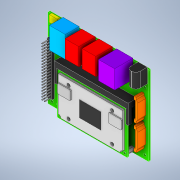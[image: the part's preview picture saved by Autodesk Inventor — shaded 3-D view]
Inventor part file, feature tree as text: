
AUTODESK INVENTOR PART (.ipt)
format: ipt  version: 2022 (Build 260153000, 153)  size: 630,784 bytes
history: native  units: mm
features: extrude x20, sketch x20, other x6, fillet x4, pattern_linear x1
ambient origin geometry x8: Origin, YZ Plane, XZ Plane, XY Plane, X Axis, Y Axis, Z Axis, Center Point
bodies: Solid1 (feature_tree), Solid2 (feature_tree), Solid3 (feature_tree), Solid4 (feature_tree), Solid5 (feature_tree), Solid6 (feature_tree), Solid8 (feature_tree), Solid9 (feature_tree), Solid10 (feature_tree)
feature tree (51):
  extrude  "Extrusion1"  Depth=79.0mm
  extrude  "Extrusion2"  Depth=6.0mm
  fillet  "Fillet1"  Radius=2.75mm
  extrude  "Extrusion3"  Depth=2.75mm
  extrude  "Extrusion4"  Depth=4.0mm
  pattern_linear  "Rectangular Pattern1"  Count1=20 Spacing1=2.54mm
  extrude  "Extrusion5"  Depth=2.75mm
  extrude  "Extrusion6"  Depth=20.2mm
  extrude  "Extrusion7"  Depth=16.2mm
  fillet  "Fillet2"  Radius=3.6mm
  extrude  "Extrusion8"  Depth=3.6mm
  extrude  "Extrusion9"  Depth=4.0mm
  extrude  "Extrusion10"  Depth=4.0mm
  extrude  "Extrusion11"  Depth=6.69mm TaperAngle=0.0deg
  fillet  "Fillet3"  Radius=5.5mm
  extrude  "Extrusion12"  Depth=73.0mm
  extrude  "Extrusion13"  Depth=63.6mm
  extrude  "Extrusion14"  Depth=31.8mm
  extrude  "Extrusion15"  Depth=45.45mm
  extrude  "Extrusion16"  Depth=9.15mm TaperAngle=0.0deg
  extrude  "Extrusion17"  Depth=69.6mm
  extrude  "Extrusion18"  Depth=0.75mm
  extrude  "Extrusion19"  Depth=3.0mm
  extrude  "Extrusion20"  Depth=1.2mm TaperAngle=0.0deg
  fillet  "Fillet4"  Radius=0.6mm
  sketch  "Sketch1"  dims[d0=100.0mm d1=79.0mm]
  sketch  "Sketch2"  dims[d2=1.57mm d3=0.0mm d4=6.0mm d5=2.75mm]
  sketch  "Sketch3"  dims[d6=2.75mm d7=2.75mm]
  sketch  "Sketch4"  dims[d8=4.0mm d9=17.0mm]
  sketch  "Sketch5"  dims[d10=29.0mm]
  sketch  "Sketch6"  dims[d11=4.0mm]
  sketch  "Sketch8"  dims[d12=0.0mm d13=0.0mm]
  sketch  "Sketch9"  dims[d14=0.6mm]
  sketch  "Sketch10"  dims[d15=1.46mm]
  sketch  "Sketch11"  dims[d16=7.46mm]
  sketch  "Sketch12"  dims[d17=5.08mm]
  sketch  "Sketch13"  dims[d18=50.8mm]
  sketch  "Sketch14"  dims[d19=2.54mm d20=0.0mm]
  other  "CAMERA_CONNECTORS"
  sketch  "Sketch15"  dims[d21=0.64mm]
  sketch  "Sketch16"  dims[d22=0.64mm]
  sketch  "Sketch17"  dims[d23=0.95mm]
  other  "USB_MINI"
  sketch  "Sketch18"  dims[d24=0.95mm]
  other  "ETHERNET"
  sketch  "Sketch19"  dims[d25=6.06mm d26=0.0mm d27=200.0mm d29=2.54mm]
  other  "USB"
  sketch  "Sketch20"  dims[d30=20.0mm d32=2.54mm d33=2.75mm]
  other  "HDMI_DISPLAYPORT"
  sketch  "Sketch21"  dims[d34=2.75mm d35=20.2mm d36=16.2mm d37=3.6mm d38=3.6mm d39=4.0mm d40=4.0mm d41=6.69mm d42=0.0mm d43=5.5mm d44=73.0mm d45=63.6mm d46=31.8mm d47=45.45mm d48=9.15mm d49=0.0mm d50=69.6mm d51=0.75mm d52=3.0mm d53=1.2mm d54=0.0mm d55=0.6mm d56=1.26mm d57=1.26mm d58=2.0mm d59=36.5mm d60=73.0mm d61=13.7mm d62=0.0mm d63=5.0mm d64=5.0mm d65=2.7mm d66=2.7mm d67=2.0mm d68=0.0mm d69=21.6mm d70=16.14mm d71=28.67mm d72=24.0mm d73=0.245mm d74=0.0mm d75=15.95mm d76=32.7mm d77=12.6mm d78=9.4mm d79=10.8mm d80=1.0mm d81=0.0mm d82=1.0mm d83=3.2mm d84=13.2mm d85=35.0mm d86=3.2mm d87=6.2mm d88=13.2mm d89=10.8mm d90=0.0mm d91=0.0mm d92=22.4mm d93=22.4mm d94=3.9mm d95=3.9mm d96=2.6mm d97=9.3mm d98=3.15mm d99=7.776mm d100=0.0mm d101=2.5mm d102=2.5mm d103=3.0mm d104=3.0mm d105=3.0mm d106=3.0mm d107=3.0mm d108=0.0mm d109=25.307274mm d110=25.307274mm d111=4.0mm d112=4.0mm d113=1.5mm d114=2.6mm d115=1.3mm d116=3.0mm d117=0.0mm d118=8.0mm d119=6.6mm d120=6.0mm d121=4.0mm d122=2.7mm d123=0.0mm d124=15.1mm d125=18.85mm d126=21.35mm d127=15.9mm d128=13.65mm d129=0.0mm d130=13.65mm d131=17.4mm d132=33.525mm d133=15.75mm d134=1.625mm d135=16.566mm d136=0.0mm d137=16.06mm d138=18.25mm d139=15.715mm d140=16.225mm d141=18.176mm d142=0.0mm d143=9.0mm d144=14.4mm d145=1.5mm d146=11.4mm d147=0.0mm d148=12.9mm d149=4.25mm]
  other  "DC_JACK"
